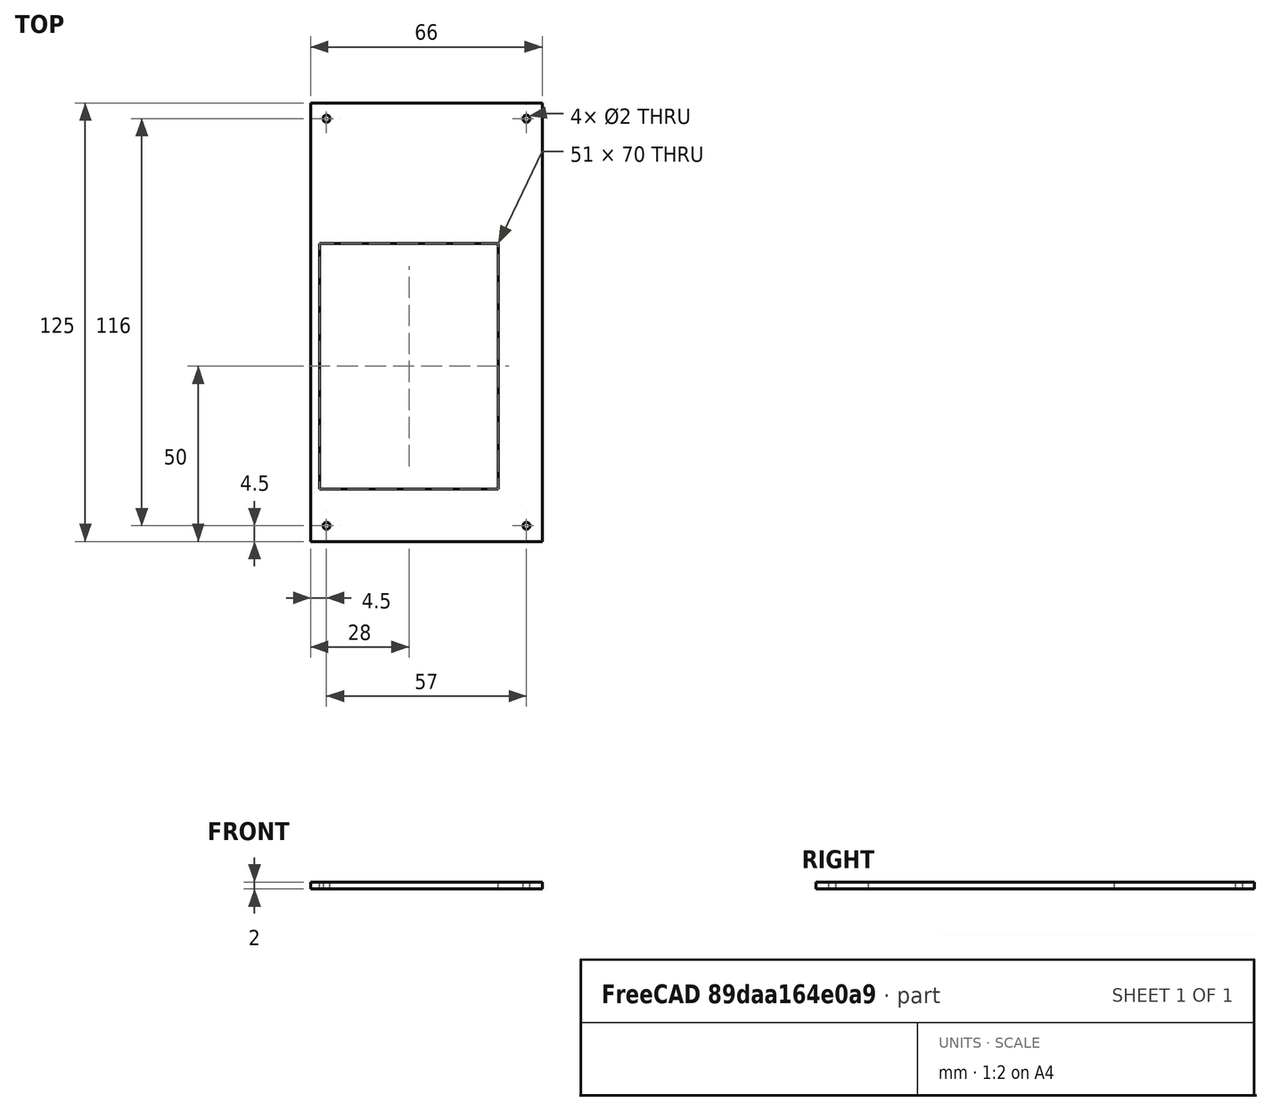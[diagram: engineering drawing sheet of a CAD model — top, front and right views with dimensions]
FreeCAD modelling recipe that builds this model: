
FCSTD DOCUMENT  (FreeCAD 0.18R16131 (Git))
Label: top
License: All rights reserved
LicenseURL: http://en.wikipedia.org/wiki/All_rights_reserved
objects: Sketcher::SketchObject×1, PartDesign::Pad×1, PartDesign::Body×1
note: 4 computed .brp shape members not serialized (recipe doc carries the construction recipe); baked Part::Feature solids carry a one-line shape summary decoded from their .brp

FEATURE [Sketcher::SketchObject] Sketch
  MapMode = 5
  Support = -> [XY_Plane]
  sketch-geometry (20):
    g0: LineSegment StartX=-33 StartY=62.5 StartZ=0 EndX=33 EndY=62.5 EndZ=0
    g1: LineSegment StartX=33 StartY=62.5 StartZ=0 EndX=33 EndY=-62.5 EndZ=0
    g2: LineSegment StartX=33 StartY=-62.5 StartZ=0 EndX=-33 EndY=-62.5 EndZ=0
    g3: LineSegment StartX=-33 StartY=-62.5 StartZ=0 EndX=-33 EndY=62.5 EndZ=0
    g4: LineSegment StartX=-30.5 StartY=22.5 StartZ=0 EndX=20.5 EndY=22.5 EndZ=0
    g5: LineSegment StartX=20.5 StartY=22.5 StartZ=0 EndX=20.5 EndY=-47.5 EndZ=0
    g6: LineSegment StartX=20.5 StartY=-47.5 StartZ=0 EndX=-30.5 EndY=-47.5 EndZ=0
    g7: LineSegment StartX=-30.5 StartY=-47.5 StartZ=0 EndX=-30.5 EndY=22.5 EndZ=0
    g8: LineSegment [constr] StartX=-28.5 StartY=62.5 StartZ=0 EndX=-28.5 EndY=58 EndZ=0
    g9: LineSegment [constr] StartX=-28.5 StartY=58 StartZ=0 EndX=-33 EndY=58 EndZ=0
    g10: LineSegment [constr] StartX=28.5 StartY=62.5 StartZ=0 EndX=28.5 EndY=58 EndZ=0
    g11: LineSegment [constr] StartX=28.5 StartY=58 StartZ=0 EndX=33 EndY=58 EndZ=0
    g12: LineSegment [constr] StartX=-33 StartY=-58 StartZ=0 EndX=-28.5 EndY=-58 EndZ=0
    g13: LineSegment [constr] StartX=-28.5 StartY=-58 StartZ=0 EndX=-28.5 EndY=-62.5 EndZ=0
    g14: LineSegment [constr] StartX=33 StartY=-58 StartZ=0 EndX=28.5 EndY=-58 EndZ=0
    g15: LineSegment [constr] StartX=28.5 StartY=-58 StartZ=0 EndX=28.5 EndY=-62.5 EndZ=0
    g16: Circle CenterX=-28.5 CenterY=-58 CenterZ=0 NormalX=0 NormalY=0 NormalZ=1 AngleXU=0 Radius=1
    g17: Circle CenterX=-28.5 CenterY=58 CenterZ=0 NormalX=0 NormalY=0 NormalZ=1 AngleXU=0 Radius=1
    g18: Circle CenterX=28.5 CenterY=58 CenterZ=0 NormalX=0 NormalY=0 NormalZ=1 AngleXU=0 Radius=1
    g19: Circle CenterX=28.5 CenterY=-58 CenterZ=0 NormalX=0 NormalY=0 NormalZ=1 AngleXU=0 Radius=1
  constraints (58):
    c: Coincident(g0,g1)
    c: Coincident(g1,g2)
    c: Coincident(g2,g3)
    c: Coincident(g3,g0)
    c: Horizontal(g2)
    c: Vertical(g3)
    c: Symmetric(g0,g0,g-2)
    c: Symmetric(g0,g1,g-1)
    c: DistanceX(g0,g0) = 66
    c: DistanceY(g1,g1) = 125
    c: Coincident(g4,g5)
    c: Coincident(g5,g6)
    c: Coincident(g6,g7)
    c: Coincident(g7,g4)
    c: Horizontal(g4)
    c: Horizontal(g6)
    c: Vertical(g5)
    c: Vertical(g7)
    c: DistanceY(g7,g7) = 70
    c: DistanceX(g4,g4) = 51
    c: Distance(g5,g2) = 15
    c: Distance(g4,g3) = 2.5
    c: PointOnObject(g8,g0)
    c: Vertical(g8)
    c: Coincident(g9,g8)
    c: PointOnObject(g9,g3)
    c: Horizontal(g9)
    c: PointOnObject(g10,g0)
    c: Vertical(g10)
    c: Horizontal(g11)
    c: Coincident(g11,g10)
    c: PointOnObject(g11,g1)
    c: PointOnObject(g12,g3)
    c: Horizontal(g12)
    c: Coincident(g13,g12)
    c: PointOnObject(g13,g2)
    c: Vertical(g13)
    c: PointOnObject(g14,g1)
    c: Horizontal(g14)
    c: Coincident(g15,g14)
    c: PointOnObject(g15,g2)
    c: Vertical(g15)
    c: Equal(g14,g15)
    c: Equal(g15,g12)
    c: Equal(g12,g13)
    c: Equal(g13,g8)
    c: Equal(g8,g9)
    c: Equal(g9,g10)
    c: Equal(g10,g11)
    c: DistanceY(g13,g13) = 4.5
    c: Coincident(g16,g12)
    c: Radius(g16) = 1
    c: Coincident(g17,g8)
    c: Coincident(g18,g10)
    c: Coincident(g19,g14)
    c: Equal(g19,g16)
    c: Equal(g18,g17)
    c: Equal(g17,g16)
FEATURE [PartDesign::Pad] Pad
  Length = 2
  Length2 = 100
  Profile = -> Sketch
  Refine = true
  Type = 0
FEATURE [PartDesign::Body] Body  label="top"
  Group = -> [Sketch,Pad]
  Origin = -> Origin
  Tip = -> Pad
